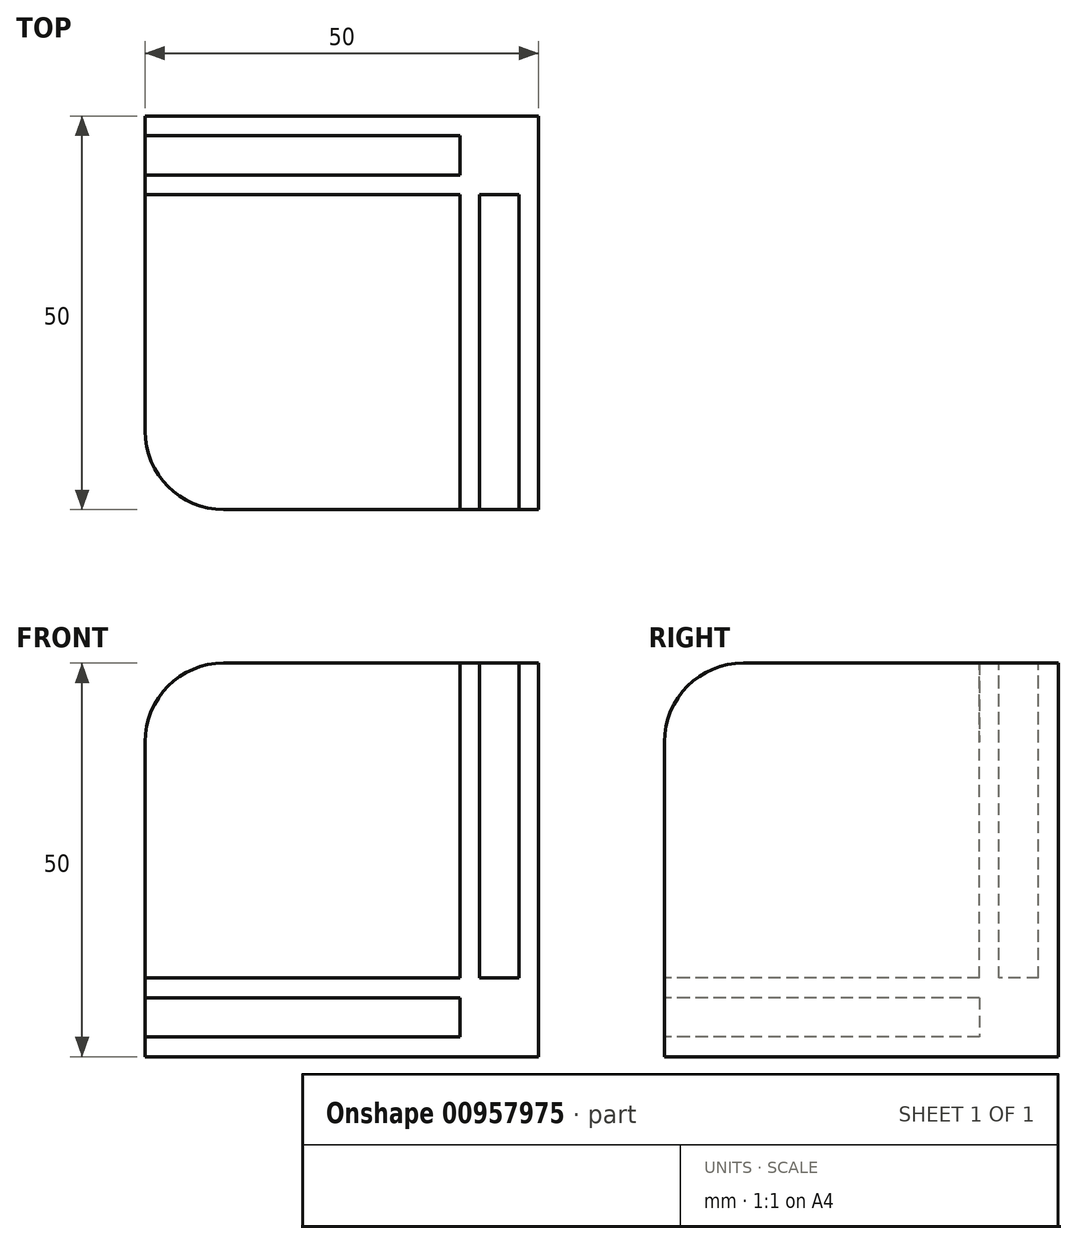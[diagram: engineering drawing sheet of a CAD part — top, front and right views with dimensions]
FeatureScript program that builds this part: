
annotation { "Feature Type Name" : "Feature", "Feature Type Description" : "" }
export const myFeature = defineFeature(function(context is Context, id is Id, definition is map)
    precondition{}
    {
        {
            var Q0;
            Q0=qCreatedBy(makeId("Top.planeOp"),FACE);
            var sketch = newSketch(context, id + "F0", { "sketchPlane" : qUnion([Q0])});
            skLineSegment(sketch, "E0.bottom", {"start": v(0, 0) * mm, "end": v(-50, 0) * mm});
            skLineSegment(sketch, "E0.top", {"start": v(0, -50) * mm, "end": v(-40, -50) * mm});
            skLineSegment(sketch, "E0.left", {"start": v(0, 0) * mm, "end": v(0, -50) * mm});
            skLineSegment(sketch, "E0.right", {"start": v(-50, 0) * mm, "end": v(-50, -40) * mm});
            skPoint(sketch, "E1.visualSharp", {"position": v(-50, -50) * mm});
            skArc(sketch, "E1.filletArc", {"start": v(-50, -40) * mm, "mid": v(-47.07, -47.07) * mm, "end": v(-40, -50) * mm});
            skSolve(sketch);
        }
        {
            var Q0;
            Q0=makeQuery(id+"F0.imprint","IMPRINT",FACE,{"disambiguationData":[TD([[makeQuery(id+"F0.imprint","IMPRINT",EDGE,{"derivedFrom":sQuery(id+"F0.wireOp",EDGE,"tNkWgY0K-5FoM-fzsk-HCrw-KOSka2LcS9h1.bottom")}),-1.0]])]});
            var Q1;
            Q1=makeQuery(id+"F0.imprint","IMPRINT",FACE,{"disambiguationData":[TD([[makeQuery(id+"F0.imprint","IMPRINT",EDGE,{"derivedFrom":sQuery(id+"F0.wireOp",EDGE,"E0.bottom")}),1.0]])]});
            var Q2;
            Q2=makeQuery(id+"F0.imprint","IMPRINT",FACE,{"disambiguationData":[TD([[makeQuery(id+"F0.imprint","IMPRINT",EDGE,{"derivedFrom":sQuery(id+"F0.wireOp",EDGE,"E0.top")}),-1.0]])]});
            var Q3;
            Q3=makeQuery(id+"F0.imprint","IMPRINT",FACE,{"disambiguationData":[TD([[makeQuery(id+"F0.imprint","IMPRINT",EDGE,{"derivedFrom":sQuery(id+"F0.wireOp",EDGE,"fvIwUqZD-S5C8-yHxi-N0ak-uGxWySerV2bo.bottom")}),1.0]])]});
            var Q4;
            Q4=makeQuery(id+"F0.imprint","IMPRINT",FACE,{"disambiguationData":[TD([[makeQuery(id+"F0.imprint","IMPRINT",EDGE,{"derivedFrom":sQuery(id+"F0.wireOp",EDGE,"JSCxDXyh-nDxv-V0qH-dKlW-7TGNpykFalIj.bottom")}),1.0]])]});
            extrude(context, id + "F1", {"entities" : qUnion([Q0, Q1, Q2, Q3, Q4]), "depth" : 10 * mm, "offsetDistance" : 25 * mm});
        }
        {
            var Q0;
            Q0=qCreatedBy(makeId("Right.planeOp"),FACE);
            var sketch = newSketch(context, id + "F2", { "sketchPlane" : qUnion([Q0])});
            skLineSegment(sketch, "E2.bottom", {"start": v(0, 10) * mm, "end": v(-50, 10) * mm});
            skLineSegment(sketch, "E2.top", {"start": v(0, 50) * mm, "end": v(-40, 50) * mm});
            skLineSegment(sketch, "E2.left", {"start": v(0, 10) * mm, "end": v(0, 50) * mm});
            skLineSegment(sketch, "E2.right", {"start": v(-50, 10) * mm, "end": v(-50, 40) * mm});
            skPoint(sketch, "E3.visualSharp", {"position": v(-50, 50) * mm});
            skArc(sketch, "E3.filletArc", {"start": v(-40, 50) * mm, "mid": v(-47.07, 47.07) * mm, "end": v(-50, 40) * mm});
            skSolve(sketch);
        }
        {
            var Q0;
            Q0=makeQuery(id+"F2.imprint","IMPRINT",FACE,{"disambiguationData":[TD([[makeQuery(id+"F2.imprint","IMPRINT",EDGE,{"derivedFrom":sQuery(id+"F2.wireOp",EDGE,"E2.bottom")}),-1.0]])]});
            extrude(context, id + "F3", {"entities" : qUnion([Q0]), "operationType" : NewBodyOperationType.ADD, "oppositeDirection" : true, "depth" : 10 * mm, "offsetDistance" : 25 * mm});
        }
        {
            var Q0;
            Q0=qCreatedBy(makeId("Front.planeOp"),FACE);
            var sketch = newSketch(context, id + "F4", { "sketchPlane" : qUnion([Q0])});
            skLineSegment(sketch, "E4.bottom", {"start": v(-10, 10) * mm, "end": v(-50, 10) * mm});
            skLineSegment(sketch, "E4.top", {"start": v(-10, 50) * mm, "end": v(-40, 50) * mm});
            skLineSegment(sketch, "E4.left", {"start": v(-10, 10) * mm, "end": v(-10, 50) * mm});
            skLineSegment(sketch, "E4.right", {"start": v(-50, 10) * mm, "end": v(-50, 40) * mm});
            skPoint(sketch, "E5.visualSharp", {"position": v(-50, 50) * mm});
            skArc(sketch, "E5.filletArc", {"start": v(-40, 50) * mm, "mid": v(-47.07, 47.07) * mm, "end": v(-50, 40) * mm});
            skSolve(sketch);
        }
        {
            var Q0;
            Q0=makeQuery(id+"F4.imprint","IMPRINT",FACE,{"disambiguationData":[TD([[makeQuery(id+"F4.imprint","IMPRINT",EDGE,{"derivedFrom":sQuery(id+"F4.wireOp",EDGE,"E4.bottom")}),-1.0]])]});
            extrude(context, id + "F5", {"entities" : qUnion([Q0]), "operationType" : NewBodyOperationType.ADD, "depth" : 10 * mm, "offsetDistance" : 25 * mm});
        }
        {
            var Q0;
            Q0=makeQuery(id+"F3.boolean.opBoolean","MERGE",FACE,{"derivedFrom":[makeQuery(id+"F1.opExtrude","SWEPT_FACE",FACE,{"disambiguationData":[OSD([sQuery(id+"F0.wireOp",EDGE,"E0.top")])]}),makeQuery(id+"F3.opExtrude","SWEPT_FACE",FACE,{"disambiguationData":[OSD([sQuery(id+"F2.wireOp",EDGE,"E2.right")])]})]});
            var sketch = newSketch(context, id + "F6", { "sketchPlane" : qUnion([Q0])});
            skLineSegment(sketch, "E6.bottom", {"start": v(-10, 2.5) * mm, "end": v(-60, 2.5) * mm});
            skLineSegment(sketch, "E6.top", {"start": v(-10, 7.5) * mm, "end": v(-60, 7.5) * mm});
            skLineSegment(sketch, "E6.left", {"start": v(-10, 2.5) * mm, "end": v(-10, 7.5) * mm});
            skLineSegment(sketch, "E6.right", {"start": v(-60, 2.5) * mm, "end": v(-60, 7.5) * mm});
            skLineSegment(sketch, "E7.bottom", {"start": v(-10, 2.5) * mm, "end": v(-15, 2.5) * mm});
            skLineSegment(sketch, "E7.top", {"start": v(-10, 52.5) * mm, "end": v(-15, 52.5) * mm});
            skLineSegment(sketch, "E8.bottom", {"start": v(-2.5, 10) * mm, "end": v(-7.5, 10) * mm});
            skLineSegment(sketch, "E8.top", {"start": v(-2.5, 60) * mm, "end": v(-7.5, 60) * mm});
            skLineSegment(sketch, "E8.left", {"start": v(-2.5, 10) * mm, "end": v(-2.5, 60) * mm});
            skLineSegment(sketch, "E8.right", {"start": v(-7.5, 10) * mm, "end": v(-7.5, 60) * mm});
            skSolve(sketch);
        }
        {
            var Q0;
            {var subQ0=sQuery(id+"F6.wireOp",EDGE,"E6.left");Q0=makeQuery(id+"F6.imprint","IMPRINT",FACE,{"disambiguationData":[TD([[makeQuery(id+"F6.imprint","IMPRINT",EDGE,{"derivedFrom":subQ0}),1.0]])]});}
            var Q1;
            {var subQ0=sQuery(id+"F6.wireOp",EDGE,"E6.right");Q1=makeQuery(id+"F6.imprint","IMPRINT",FACE,{"disambiguationData":[TD([[makeQuery(id+"F6.imprint","IMPRINT",EDGE,{"derivedFrom":subQ0}),-1.0]])]});}
            var Q2;
            {var subQ0=sQuery(id+"F6.wireOp",EDGE,"E6.right");Q2=makeQuery(id+"F6.imprint","IMPRINT",FACE,{"disambiguationData":[TD([[makeQuery(id+"F6.imprint","IMPRINT",EDGE,{"derivedFrom":subQ0}),-1.0]])]});}
            var Q3;
            {var subQ0=sQuery(id+"F6.wireOp",EDGE,"E8.bottom");Q3=makeQuery(id+"F6.imprint","IMPRINT",FACE,{"disambiguationData":[TD([[makeQuery(id+"F6.imprint","IMPRINT",EDGE,{"derivedFrom":subQ0}),-1.0]])]});}
            var Q4;
            {var subQ0=sQuery(id+"F6.wireOp",EDGE,"E8.top");Q4=makeQuery(id+"F6.imprint","IMPRINT",FACE,{"disambiguationData":[TD([[makeQuery(id+"F6.imprint","IMPRINT",EDGE,{"derivedFrom":subQ0}),1.0]])]});}
            extrude(context, id + "F7", {"entities" : qUnion([Q0, Q1, Q2, Q3, Q4]), "operationType" : NewBodyOperationType.REMOVE, "oppositeDirection" : true, "depth" : 40 * mm, "offsetDistance" : 25 * mm});
        }
        {
            var Q0;
            Q0=makeQuery(id+"F5.boolean.opBoolean","MERGE",FACE,{"derivedFrom":[makeQuery(id+"F3.opExtrude","SWEPT_FACE",FACE,{"disambiguationData":[OSD([sQuery(id+"F2.wireOp",EDGE,"E2.top")])]}),makeQuery(id+"F5.opExtrude","SWEPT_FACE",FACE,{"disambiguationData":[OSD([sQuery(id+"F4.wireOp",EDGE,"E4.top")])]})]});
            var sketch = newSketch(context, id + "F8", { "sketchPlane" : qUnion([Q0])});
            skLineSegment(sketch, "E9.bottom", {"start": v(-10, -2.5) * mm, "end": v(-60, -2.5) * mm});
            skLineSegment(sketch, "E9.top", {"start": v(-10, -7.5) * mm, "end": v(-60, -7.5) * mm});
            skLineSegment(sketch, "E9.left", {"start": v(-10, -2.5) * mm, "end": v(-10, -7.5) * mm});
            skLineSegment(sketch, "E9.right", {"start": v(-60, -2.5) * mm, "end": v(-60, -7.5) * mm});
            skSolve(sketch);
        }
        {
            var Q0;
            {var subQ0=sQuery(id+"F8.wireOp",EDGE,"E9.left");Q0=makeQuery(id+"F8.imprint","IMPRINT",FACE,{"disambiguationData":[TD([[makeQuery(id+"F8.imprint","IMPRINT",EDGE,{"derivedFrom":subQ0}),-1.0]])]});}
            var Q1;
            {var subQ0=sQuery(id+"F8.wireOp",EDGE,"E9.right");Q1=makeQuery(id+"F8.imprint","IMPRINT",FACE,{"disambiguationData":[TD([[makeQuery(id+"F8.imprint","IMPRINT",EDGE,{"derivedFrom":subQ0}),1.0]])]});}
            extrude(context, id + "F9", {"entities" : qUnion([Q0, Q1]), "operationType" : NewBodyOperationType.REMOVE, "oppositeDirection" : true, "depth" : 40 * mm, "offsetDistance" : 25 * mm});
        }
    });
